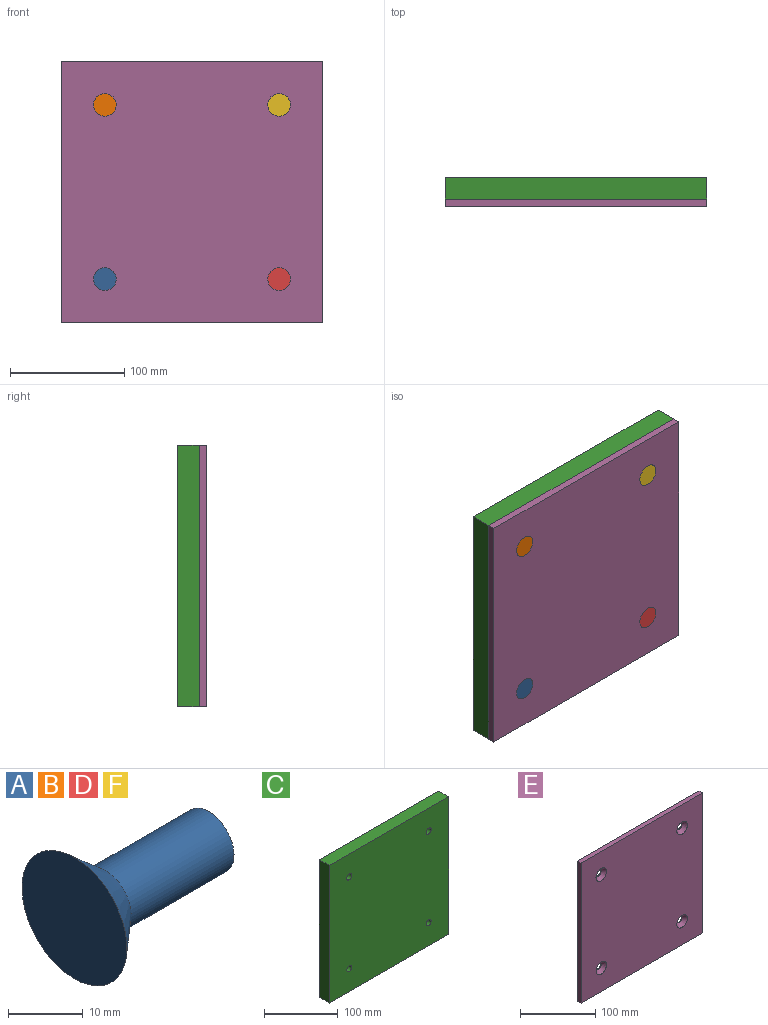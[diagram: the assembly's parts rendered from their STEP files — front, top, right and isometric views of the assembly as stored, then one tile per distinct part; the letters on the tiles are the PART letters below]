
ASSEMBLY  parts=6 mates=5
PART A: 4 faces, bbox 25.4x19.8x19.8 mm
  f0: plane 9.53x9.53mm, normal (1,0,0), area 71.3mm2, adj f1
  f1: cylinder r=4.76mm len=19.47mm, axis (1,0,0), area 582.6mm2, adj f0,f2
  f2: cone r=9.92mm half-angle=41deg, axis (-1,0,0), area 362.5mm2, adj f1,f3
  f3: plane 19.84x19.84mm, normal (-1,0,0), area 309.1mm2, adj f2
PART B: same geometry as A
PART C: 10 faces, bbox 228.6x19.1x228.6 mm
  f0: plane 228.6x19.05mm, normal (0,0,-1), area 4354.8mm2, adj f1,f3,f4,f5
  f1: plane 228.6x19.05mm, normal (1,0,0), area 4354.8mm2, adj f0,f2,f4,f5
  f2: plane 228.6x19.05mm, normal (0,0,1), area 4354.8mm2, adj f1,f3,f4,f5
  f3: plane 228.6x19.05mm, normal (-1,0,0), area 4354.8mm2, adj f0,f2,f4,f5
  f4: plane 228.6x228.6mm, normal (0,-1,0), area 51972.9mm2, adj f0,f1,f2,f3,f6,f7,f8,f9
  f5: plane 228.6x228.6mm, normal (0,1,0), area 51972.9mm2, adj f0,f1,f2,f3,f6,f7,f8,f9
  f6: cylinder r=4.76mm len=19.05mm, axis (0,-1,0), area 570mm2, adj f4,f5
  f7: cylinder r=4.76mm len=19.05mm, axis (0,-1,0), area 570mm2, adj f4,f5
  f8: cylinder r=4.76mm len=19.05mm, axis (0,-1,0), area 570mm2, adj f4,f5
  f9: cylinder r=4.76mm len=19.05mm, axis (0,-1,0), area 570mm2, adj f4,f5
PART D: same geometry as A
PART E: 14 faces, bbox 228.6x6.4x228.6 mm
  f0: plane 228.6x6.35mm, normal (0,0,-1), area 1451.6mm2, adj f1,f3,f4,f5
  f1: plane 228.6x6.35mm, normal (1,0,0), area 1451.6mm2, adj f0,f2,f4,f5
  f2: plane 228.6x6.35mm, normal (0,0,1), area 1451.6mm2, adj f1,f3,f4,f5
  f3: plane 228.6x6.35mm, normal (-1,0,0), area 1451.6mm2, adj f0,f2,f4,f5
  f4: plane 228.6x228.6mm, normal (0,-1,0), area 51021.7mm2, adj f0,f1,f2,f3,f7,f9,f11,f13
  f5: plane 228.6x228.6mm, normal (0,1,0), area 51972.9mm2, adj f0,f1,f2,f3,f6,f8,f10,f12
  f6: cylinder r=4.76mm len=9.53mm, axis (0,-1,0), area 35.7mm2, adj f5,f7
  f7: cone r=4.76mm half-angle=45deg, axis (0,-1,0), area 336.3mm2, adj f4,f6
  f8: cylinder r=4.76mm len=9.53mm, axis (0,-1,0), area 35.7mm2, adj f5,f9
  f9: cone r=4.76mm half-angle=45deg, axis (0,-1,0), area 336.3mm2, adj f4,f8
  f10: cylinder r=4.76mm len=9.53mm, axis (0,-1,0), area 35.7mm2, adj f5,f11
  f11: cone r=4.76mm half-angle=45deg, axis (0,-1,0), area 336.3mm2, adj f4,f10
  f12: cylinder r=4.76mm len=9.53mm, axis (0,-1,0), area 35.7mm2, adj f5,f13
  f13: cone r=4.76mm half-angle=45deg, axis (0,-1,0), area 336.3mm2, adj f4,f12
PART F: same geometry as A
PLACE A rot(axis=(0,0,1),90deg) t=(-76.2,18.46,-76.2)mm
PLACE B rot(axis=(0,0,1),90deg) t=(-76.2,18.46,76.2)mm
PLACE C t=(0,19.05,0)mm
PLACE D rot(axis=(0,0,1),90deg) t=(76.2,18.46,-76.2)mm
PLACE E t=(0,-3.18,0)mm
PLACE F rot(axis=(0,0,1),90deg) t=(76.2,18.46,76.2)mm
MATE parallel A.f1 <-> C.f9  axis (0,1,0) through (-76.2,19.05,-76.2)mm
MATE fastened C.f4 <-> E.f5  axis (0,-1,0) through (0,0,0)mm
MATE parallel B.f1 <-> C.f6  axis (0,1,0) through (-76.2,19.05,76.2)mm
MATE parallel D.f1 <-> C.f8  axis (0,1,0) through (76.2,19.05,-76.2)mm
MATE parallel F.f1 <-> C.f7  axis (0,1,0) through (76.2,19.05,76.2)mm
